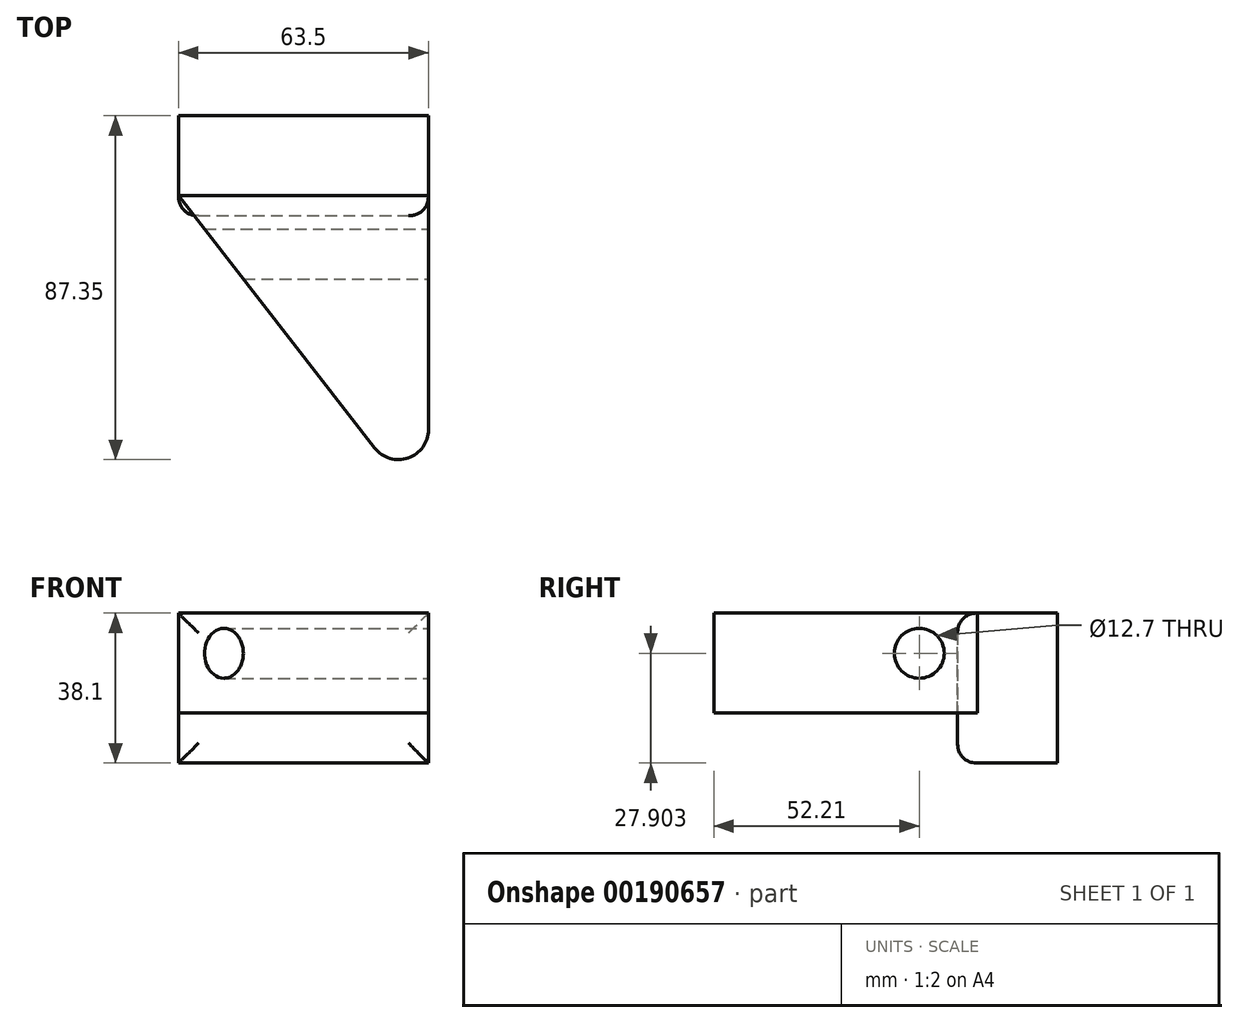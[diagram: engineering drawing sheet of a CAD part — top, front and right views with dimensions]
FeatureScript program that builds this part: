
annotation { "Feature Type Name" : "Feature", "Feature Type Description" : "" }
export const myFeature = defineFeature(function(context is Context, id is Id, definition is map)
    precondition{}
    {
        {
            var Q0;
            Q0=qCreatedBy(makeId("Front.planeOp"),FACE);
            var sketch = newSketch(context, id + "F0", { "sketchPlane" : qUnion([Q0])});
            skLineSegment(sketch, "E0.bottom", {"start": v(0, 0) * mm, "end": v(63.5, 0) * mm});
            skLineSegment(sketch, "E0.top", {"start": v(0, 38.1) * mm, "end": v(63.5, 38.1) * mm});
            skLineSegment(sketch, "E0.left", {"start": v(0, 0) * mm, "end": v(0, 38.1) * mm});
            skLineSegment(sketch, "E0.right", {"start": v(63.5, 0) * mm, "end": v(63.5, 38.1) * mm});
            skSolve(sketch);
        }
        {
            var Q0;
            Q0=makeQuery(id+"F0.imprint","IMPRINT",FACE,{"disambiguationData":[TD([[makeQuery(id+"F0.imprint","IMPRINT",EDGE,{"derivedFrom":sQuery(id+"F0.wireOp",EDGE,"E0.bottom")}),1.0]])]});
            extrude(context, id + "F1", {"entities" : qUnion([Q0]), "depth" : 25.4 * mm});
        }
        {
            var Q0;
            Q0=makeQuery(id+"F1.opExtrude","CAP_FACE",FACE,{"disambiguationData":[OSD([sQuery(id+"F0.wireOp",EDGE,"E0.bottom"),sQuery(id+"F0.wireOp",EDGE,"E0.top"),sQuery(id+"F0.wireOp",EDGE,"E0.left"),sQuery(id+"F0.wireOp",EDGE,"E0.right")])],"isStart":false});
            fillet(context, id + "F2", {"entities" : qUnion([Q0]), "radius" : 5.08 * mm, "tangentPropagation" : true, "rho" : .45, "crossSection" : FilletCrossSection.CONIC, "allowEdgeOverflow" : false});
        }
        {
            var Q0;
            Q0=makeQuery(id+"F1.opExtrude","SWEPT_FACE",FACE,{"disambiguationData":[OSD([sQuery(id+"F0.wireOp",EDGE,"E0.top")])]});
            var sketch = newSketch(context, id + "F3", { "sketchPlane" : qUnion([Q0])});
            skLineSegment(sketch, "E1", {"start": v(63.5, -101.93) * mm, "end": v(63.5, -20.32) * mm});
            skLineSegment(sketch, "E2", {"start": v(63.5, -20.32) * mm, "end": v(0, -20.32) * mm});
            skLineSegment(sketch, "E3", {"start": v(0, -20.32) * mm, "end": v(63.5, -101.93) * mm});
            skSolve(sketch);
        }
        {
            var Q0;
            Q0 = qSketchRegion(id + "F3", true);
            extrude(context, id + "F4", {"entities" : qUnion([Q0]), "oppositeDirection" : true, "depth" : 25.4 * mm, "offsetDistance" : 25.4 * mm});
        }
        {
            var Q0;
            Q0=makeQuery(id+"F4.opExtrude","SWEPT_FACE",FACE,{"disambiguationData":[OSD([sQuery(id+"F3.wireOp",EDGE,"E1")])]});
            var sketch = newSketch(context, id + "F5", { "sketchPlane" : qUnion([Q0])});
            skCircle(sketch, "E4", {"center": v(-35.14, 27.9) * mm, "radius": 6.35 * mm});
            skCircle(sketch, "E5", {"center": v(-35.44, 34.25) * mm, "radius": 15.98 * mm, "construction": true});
            skSolve(sketch);
        }
        {
            var Q0;
            Q0 = qSketchRegion(id + "F5", true);
            extrude(context, id + "F6", {"entities" : qUnion([Q0]), "operationType" : NewBodyOperationType.REMOVE, "endBound" : BoundingType.UP_TO_NEXT, "oppositeDirection" : true, "depth" : 25.4 * mm, "offsetDistance" : 25.4 * mm});
        }
        {
            var Q0;
            Q0=makeQuery(id+"F4.opExtrude","SWEPT_EDGE",EDGE,{"disambiguationData":[OSD([sQuery(id+"F3.wireOp",EDGE,"E1"),sQuery(id+"F3.wireOp",EDGE,"E3")])]});
            fillet(context, id + "F7", {"entities" : qUnion([Q0]), "radius" : 7.62 * mm, "tangentPropagation" : true, "allowEdgeOverflow" : false});
        }
    });
